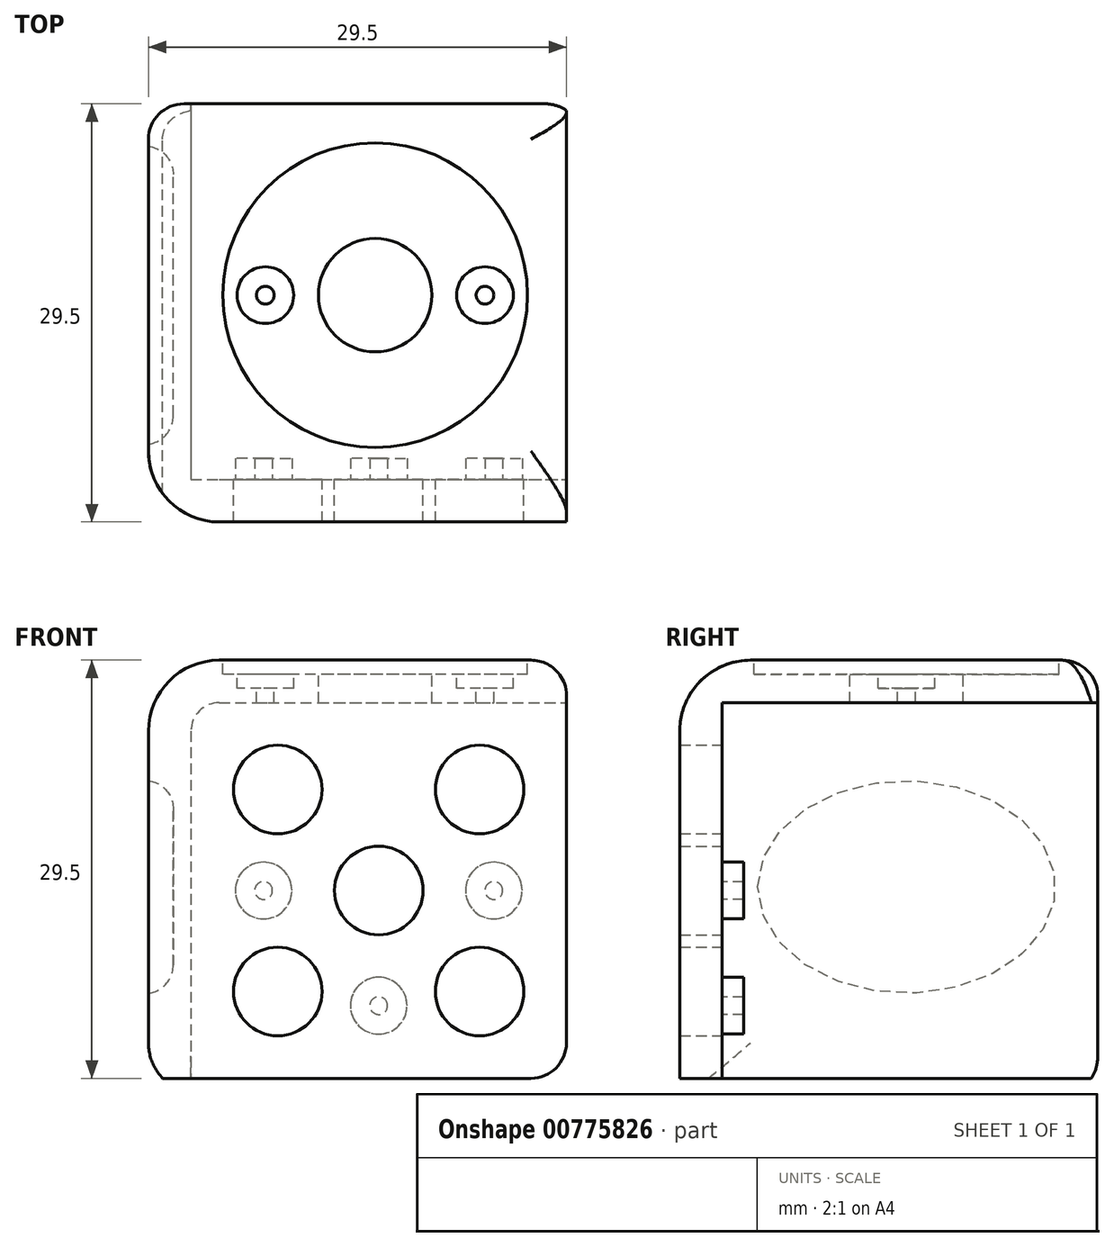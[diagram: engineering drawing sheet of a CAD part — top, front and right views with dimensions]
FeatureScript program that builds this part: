
annotation { "Feature Type Name" : "Feature", "Feature Type Description" : "" }
export const myFeature = defineFeature(function(context is Context, id is Id, definition is map)
    precondition{}
    {
        {
            var Q0;
            Q0=qCreatedBy(makeId("Front.planeOp"),FACE);
            var sketch = newSketch(context, id + "F0", { "sketchPlane" : qUnion([Q0])});
            skLineSegment(sketch, "E0.bottom", {"start": v(-9.8, 24) * mm, "end": v(13.7, 24) * mm});
            skLineSegment(sketch, "E0.top", {"start": v(-14.8, -5.5) * mm, "end": v(12.2, -5.5) * mm});
            skLineSegment(sketch, "E0.left", {"start": v(-14.8, 19) * mm, "end": v(-14.8, -5.5) * mm});
            skLineSegment(sketch, "E0.right", {"start": v(14.7, 23) * mm, "end": v(14.7, -3) * mm});
            skPoint(sketch, "E1", {"position": v(-9.3, 24) * mm});
            skPoint(sketch, "E2", {"position": v(-14.8, 18.5) * mm});
            skPoint(sketch, "E3", {"position": v(-14.8, -3) * mm});
            skPoint(sketch, "E4", {"position": v(-9.3, -5.5) * mm});
            skPoint(sketch, "E5", {"position": v(12.2, -5.5) * mm});
            skPoint(sketch, "E6", {"position": v(14.7, -3) * mm});
            skPoint(sketch, "E7", {"position": v(14.7, 18.5) * mm});
            skPoint(sketch, "E8", {"position": v(12.2, 24) * mm});
            skLineSegment(sketch, "E9", {"start": v(-9.3, 24) * mm, "end": v(-9.3, -5.5) * mm});
            skLineSegment(sketch, "E10", {"start": v(-14.8, -3) * mm, "end": v(14.7, -3) * mm});
            skLineSegment(sketch, "E11", {"start": v(12.2, -5.5) * mm, "end": v(12.2, 24) * mm});
            skLineSegment(sketch, "E12", {"start": v(14.7, 18.5) * mm, "end": v(-14.8, 18.5) * mm});
            skPoint(sketch, "E13", {"position": v(-9.3, 18.5) * mm});
            skPoint(sketch, "E14", {"position": v(12.2, 18.5) * mm});
            skPoint(sketch, "E15", {"position": v(-9.3, -3) * mm});
            skPoint(sketch, "E16", {"position": v(12.2, -3) * mm});
            skCircle(sketch, "E17", {"center": v(-5.67, 14.88) * mm, "radius": 3.12 * mm});
            skCircle(sketch, "E18", {"center": v(8.58, 14.88) * mm, "radius": 3.12 * mm});
            skCircle(sketch, "E19", {"center": v(-5.67, 0.62) * mm, "radius": 3.12 * mm});
            skCircle(sketch, "E20", {"center": v(8.58, 0.62) * mm, "radius": 3.12 * mm});
            skCircle(sketch, "E21", {"center": v(1.46, 7.75) * mm, "radius": 3.12 * mm});
            skPoint(sketch, "E22.visualSharp", {"position": v(-14.8, 24) * mm});
            skArc(sketch, "E22.filletArc", {"start": v(-9.8, 24) * mm, "mid": v(-13.33, 22.54) * mm, "end": v(-14.8, 19) * mm});
            skPoint(sketch, "E23", {"position": v(14.7, 23) * mm});
            skArc(sketch, "E24", {"start": v(14.7, 23) * mm, "mid": v(13.55, 23.74) * mm, "end": v(12.2, 24) * mm});
            skPoint(sketch, "E25", {"position": v(-13.8, -5.5) * mm});
            skArc(sketch, "E26", {"start": v(-14.8, -3) * mm, "mid": v(-14.53, -4.35) * mm, "end": v(-13.8, -5.5) * mm});
            skPoint(sketch, "E27.visualSharp", {"position": v(14.7, -5.5) * mm});
            skArc(sketch, "E27.filletArc", {"start": v(12.2, -5.5) * mm, "mid": v(13.98, -4.77) * mm, "end": v(14.7, -3) * mm});
            skSolve(sketch);
        }
        {
            var Q0;
            {var subQ7=sQuery(id+"F0.wireOp",EDGE,"E22.filletArc");Q0=makeQuery(id+"F0.imprint","IMPRINT",FACE,{"disambiguationData":[TD([[makeQuery(id+"F0.imprint","IMPRINT",EDGE,{"derivedFrom":subQ7}),1.0]])]});}
            var Q1;
            {var subQ0=sQuery(id+"F0.wireOp",EDGE,"E9");var subQ1=sQuery(id+"F0.wireOp",EDGE,"E0.bottom");var subQ2=makeQuery(id+"F0.imprint","INTERSECT",VERTEX,{"derivedFrom":[subQ1,subQ0]});Q1=makeQuery(id+"F0.imprint","IMPRINT",FACE,{"disambiguationData":[TD([[makeQuery(id+"F0.imprint","IMPRINT",EDGE,{"disambiguationData":[TD([[subQ2,-1.0]])],"derivedFrom":subQ0}),1.0]])]});}
            var Q2;
            {var subQ0=sQuery(id+"F0.wireOp",EDGE,"E24");Q2=makeQuery(id+"F0.imprint","IMPRINT",FACE,{"disambiguationData":[TD([[makeQuery(id+"F0.imprint","IMPRINT",EDGE,{"derivedFrom":subQ0}),1.0]])]});}
            var Q3;
            {var subQ0=sQuery(id+"F0.wireOp",EDGE,"E10");var subQ5=sQuery(id+"F0.wireOp",EDGE,"E11");var subQ7=makeQuery(id+"F0.imprint","INTERSECT",VERTEX,{"derivedFrom":[subQ0,subQ5]});Q3=makeQuery(id+"F0.imprint","IMPRINT",FACE,{"disambiguationData":[TD([[makeQuery(id+"F0.imprint","IMPRINT",EDGE,{"disambiguationData":[TD([[subQ7,-1.0]])],"derivedFrom":subQ5}),-1.0]])]});}
            var Q4;
            Q4=makeQuery(id+"F0.imprint","IMPRINT",FACE,{"disambiguationData":[TD([[makeQuery(id+"F0.imprint","IMPRINT",EDGE,{"derivedFrom":sQuery(id+"F0.wireOp",EDGE,"E17")}),-1.0]])]});
            var Q5;
            {var subQ3=sQuery(id+"F0.wireOp",EDGE,"E12");var subQ5=sQuery(id+"F0.wireOp",EDGE,"E9");var subQ6=makeQuery(id+"F0.imprint","INTERSECT",VERTEX,{"derivedFrom":[subQ5,subQ3]});Q5=makeQuery(id+"F0.imprint","IMPRINT",FACE,{"disambiguationData":[TD([[makeQuery(id+"F0.imprint","IMPRINT",EDGE,{"disambiguationData":[TD([[subQ6,-1.0]])],"derivedFrom":subQ5}),-1.0]])]});}
            var Q6;
            {var subQ3=sQuery(id+"F0.wireOp",EDGE,"E26");Q6=makeQuery(id+"F0.imprint","IMPRINT",FACE,{"disambiguationData":[TD([[makeQuery(id+"F0.imprint","IMPRINT",EDGE,{"derivedFrom":subQ3}),1.0]])]});}
            var Q7;
            {var subQ1=sQuery(id+"F0.wireOp",EDGE,"E0.top");var subQ3=sQuery(id+"F0.wireOp",EDGE,"E9");var subQ4=makeQuery(id+"F0.imprint","INTERSECT",VERTEX,{"derivedFrom":[subQ1,subQ3]});Q7=makeQuery(id+"F0.imprint","IMPRINT",FACE,{"disambiguationData":[TD([[makeQuery(id+"F0.imprint","IMPRINT",EDGE,{"disambiguationData":[TD([[subQ4,1.0]])],"derivedFrom":subQ3}),1.0]])]});}
            var Q8;
            {var subQ0=sQuery(id+"F0.wireOp",EDGE,"E27.filletArc");Q8=makeQuery(id+"F0.imprint","IMPRINT",FACE,{"disambiguationData":[TD([[makeQuery(id+"F0.imprint","IMPRINT",EDGE,{"derivedFrom":subQ0}),1.0]])]});}
            extrude(context, id + "F1", {"entities" : qUnion([Q0, Q1, Q2, Q3, Q4, Q5, Q6, Q7, Q8]), "depth" : 3 * mm, "offsetDistance" : 25 * mm});
        }
        {
            var Q0;
            Q0=makeQuery(id+"F1.opExtrude","CAP_FACE",FACE,{"disambiguationData":[OSD([sQuery(id+"F0.wireOp",EDGE,"E0.bottom"),sQuery(id+"F0.wireOp",EDGE,"E0.top"),sQuery(id+"F0.wireOp",EDGE,"E0.left"),sQuery(id+"F0.wireOp",EDGE,"E0.right"),sQuery(id+"F0.wireOp",EDGE,"E17"),sQuery(id+"F0.wireOp",EDGE,"E18"),sQuery(id+"F0.wireOp",EDGE,"E19"),sQuery(id+"F0.wireOp",EDGE,"E20"),sQuery(id+"F0.wireOp",EDGE,"E21"),sQuery(id+"F0.wireOp",EDGE,"E22.filletArc"),sQuery(id+"F0.wireOp",EDGE,"E24"),sQuery(id+"F0.wireOp",EDGE,"E26"),sQuery(id+"F0.wireOp",EDGE,"E27.filletArc")])],"isStart":true});
            var sketch = newSketch(context, id + "F2", { "sketchPlane" : qUnion([Q0])});
            skPoint(sketch, "E28", {"position": v(11.8, -3) * mm});
            skPoint(sketch, "E29", {"position": v(-12.2, 21) * mm});
            skLineSegment(sketch, "E30", {"start": v(-12.2, 21) * mm, "end": v(9.8, 21) * mm});
            skLineSegment(sketch, "E31", {"start": v(11.8, 19) * mm, "end": v(11.8, -3) * mm});
            skLineSegment(sketch, "E32", {"start": v(11.8, -3) * mm, "end": v(11.8, -5.5) * mm});
            skLineSegment(sketch, "E33", {"start": v(-12.2, 21) * mm, "end": v(-14.7, 21) * mm});
            skPoint(sketch, "E34.visualSharp", {"position": v(11.8, 21) * mm});
            skArc(sketch, "E34.filletArc", {"start": v(11.8, 19) * mm, "mid": v(11.2, 20.41) * mm, "end": v(9.8, 21) * mm});
            skSolve(sketch);
        }
        {
            var Q0;
            Q0=makeQuery(id+"F2.imprint","IMPRINT",FACE,{"disambiguationData":[TD([[makeQuery(id+"F2.imprint","IMPRINT",EDGE,{"derivedFrom":sQuery(id+"F2.wireOp",EDGE,"E30")}),1.0]])]});
            extrude(context, id + "F3", {"entities" : qUnion([Q0]), "operationType" : NewBodyOperationType.ADD, "depth" : 26.5 * mm, "offsetDistance" : 25 * mm});
        }
        {
            var Q0;
            Q0=makeQuery(id+"F1.opExtrude","CAP_EDGE",EDGE,{"disambiguationData":[OSD([sQuery(id+"F0.wireOp",EDGE,"E0.bottom")])],"isStart":false});
            var Q1;
            Q1=makeQuery(id+"F1.opExtrude","CAP_EDGE",EDGE,{"disambiguationData":[OSD([sQuery(id+"F0.wireOp",EDGE,"E0.left")])],"isStart":false});
            var Q2;
            Q2=makeQuery(id+"F1.opExtrude","CAP_EDGE",EDGE,{"disambiguationData":[OSD([sQuery(id+"F0.wireOp",EDGE,"E22.filletArc")])],"isStart":false});
            fillet(context, id + "F4", {"entities" : qUnion([Q0, Q1, Q2]), "radius" : 5 * mm, "tangentPropagation" : true, "allowEdgeOverflow" : false});
        }
        {
            var Q0;
            {var subQ0=sQuery(id+"F0.wireOp",EDGE,"E24");var subQ1=sQuery(id+"F0.wireOp",EDGE,"E0.right");Q0=makeQuery(id+"F3.boolean.opBoolean","MERGE",EDGE,{"derivedFrom":[makeQuery(id+"F1.opExtrude","SWEPT_EDGE",EDGE,{"disambiguationData":[OSD([subQ1,subQ0])]}),makeQuery(id+"F3.opExtrude","SWEPT_EDGE",EDGE,{"disambiguationData":[OSD([subQ1,subQ0])]})]});}
            var Q1;
            Q1=makeQuery(id+"F3.opExtrude","CAP_EDGE",EDGE,{"disambiguationData":[OSD([sQuery(id+"F0.wireOp",EDGE,"E0.bottom")])],"isStart":false});
            var Q2;
            Q2=makeQuery(id+"F3.opExtrude","CAP_EDGE",EDGE,{"disambiguationData":[OSD([sQuery(id+"F0.wireOp",EDGE,"E24")])],"isStart":false});
            fillet(context, id + "F5", {"entities" : qUnion([Q0, Q1, Q2]), "radius" : 2.5 * mm, "tangentPropagation" : true, "allowEdgeOverflow" : false});
        }
        {
            var Q0;
            {var subQ0=sQuery(id+"F0.wireOp",EDGE,"E0.bottom");Q0=makeQuery(id+"F3.boolean.opBoolean","MERGE",FACE,{"derivedFrom":[makeQuery(id+"F1.opExtrude","SWEPT_FACE",FACE,{"disambiguationData":[OSD([subQ0])]}),makeQuery(id+"F3.opExtrude","SWEPT_FACE",FACE,{"disambiguationData":[OSD([subQ0])]})]});}
            var sketch = newSketch(context, id + "F6", { "sketchPlane" : qUnion([Q0])});
            skLineSegment(sketch, "E35", {"start": v(1.2, 24) * mm, "end": v(1.2, 2) * mm});
            skLineSegment(sketch, "E36", {"start": v(-9.8, 13) * mm, "end": v(12.2, 13) * mm});
            skCircle(sketch, "E37", {"center": v(1.2, 13) * mm, "radius": 10.75 * mm});
            skSolve(sketch);
        }
        {
            var Q0;
            {var subQ0=sQuery(id+"F6.wireOp",EDGE,"E36");var subQ1=sQuery(id+"F6.wireOp",EDGE,"E35");var subQ2=makeQuery(id+"F6.imprint","INTERSECT",VERTEX,{"derivedFrom":[subQ1,subQ0]});Q0=makeQuery(id+"F6.imprint","IMPRINT",FACE,{"disambiguationData":[TD([[makeQuery(id+"F6.imprint","IMPRINT",EDGE,{"disambiguationData":[TD([[subQ2,-1.0]])],"derivedFrom":subQ1}),-1.0]])]});}
            var Q1;
            {var subQ0=sQuery(id+"F6.wireOp",EDGE,"E37");var subQ1=sQuery(id+"F6.wireOp",EDGE,"E35");var subQ2=makeQuery(id+"F6.imprint","INTERSECT",VERTEX,{"disambiguationData":[OD(0.0)],"derivedFrom":[subQ1,subQ0]});Q1=makeQuery(id+"F6.imprint","IMPRINT",FACE,{"disambiguationData":[TD([[makeQuery(id+"F6.imprint","IMPRINT",EDGE,{"disambiguationData":[TD([[subQ2,-1.0]])],"derivedFrom":subQ1}),-1.0]])]});}
            var Q2;
            {var subQ0=sQuery(id+"F6.wireOp",EDGE,"E37");var subQ1=sQuery(id+"F6.wireOp",EDGE,"E35");var subQ2=makeQuery(id+"F6.imprint","INTERSECT",VERTEX,{"disambiguationData":[OD(0.0)],"derivedFrom":[subQ1,subQ0]});Q2=makeQuery(id+"F6.imprint","IMPRINT",FACE,{"disambiguationData":[TD([[makeQuery(id+"F6.imprint","IMPRINT",EDGE,{"disambiguationData":[TD([[subQ2,-1.0]])],"derivedFrom":subQ1}),1.0]])]});}
            var Q3;
            {var subQ0=sQuery(id+"F6.wireOp",EDGE,"E36");var subQ1=sQuery(id+"F6.wireOp",EDGE,"E35");var subQ2=makeQuery(id+"F6.imprint","INTERSECT",VERTEX,{"derivedFrom":[subQ1,subQ0]});Q3=makeQuery(id+"F6.imprint","IMPRINT",FACE,{"disambiguationData":[TD([[makeQuery(id+"F6.imprint","IMPRINT",EDGE,{"disambiguationData":[TD([[subQ2,-1.0]])],"derivedFrom":subQ1}),1.0]])]});}
            extrude(context, id + "F7", {"entities" : qUnion([Q0, Q1, Q2, Q3]), "operationType" : NewBodyOperationType.REMOVE, "oppositeDirection" : true, "depth" : 1 * mm, "offsetDistance" : 25 * mm});
        }
        {
            var Q0;
            Q0=makeQuery(id+"F7.boolean.opBoolean","COPY",FACE,{"derivedFrom":makeQuery(id+"F7.opExtrude","CAP_FACE",FACE,{"disambiguationData":[OSD([sQuery(id+"F6.wireOp",EDGE,"E37")])],"isStart":false})});
            var sketch = newSketch(context, id + "F8", { "sketchPlane" : qUnion([Q0])});
            skCircle(sketch, "E38", {"center": v(1.2, 13) * mm, "radius": 4 * mm});
            skCircle(sketch, "E39", {"center": v(-6.54, 13) * mm, "radius": 2 * mm});
            skCircle(sketch, "E40", {"center": v(8.96, 13) * mm, "radius": 2 * mm});
            skCircle(sketch, "E41", {"center": v(-6.54, 13) * mm, "radius": 0.62 * mm});
            skCircle(sketch, "E42", {"center": v(8.96, 13) * mm, "radius": 0.62 * mm});
            skSolve(sketch);
        }
        {
            var Q0;
            Q0=makeQuery(id+"F8.imprint","IMPRINT",FACE,{"disambiguationData":[TD([[makeQuery(id+"F8.imprint","IMPRINT",EDGE,{"derivedFrom":sQuery(id+"F8.wireOp",EDGE,"E38")}),1.0]])]});
            extrude(context, id + "F9", {"entities" : qUnion([Q0]), "operationType" : NewBodyOperationType.REMOVE, "oppositeDirection" : true, "depth" : 25 * mm, "offsetDistance" : 25 * mm});
        }
        {
            var Q0;
            Q0=makeQuery(id+"F8.imprint","IMPRINT",FACE,{"disambiguationData":[TD([[makeQuery(id+"F8.imprint","IMPRINT",EDGE,{"derivedFrom":sQuery(id+"F8.wireOp",EDGE,"E39")}),1.0]])]});
            extrude(context, id + "F10", {"entities" : qUnion([Q0]), "operationType" : NewBodyOperationType.REMOVE, "oppositeDirection" : true, "depth" : 1 * mm, "offsetDistance" : 25 * mm});
        }
        {
            var Q0;
            Q0=makeQuery(id+"F8.imprint","IMPRINT",FACE,{"disambiguationData":[TD([[makeQuery(id+"F8.imprint","IMPRINT",EDGE,{"derivedFrom":sQuery(id+"F8.wireOp",EDGE,"E40")}),1.0]])]});
            extrude(context, id + "F11", {"entities" : qUnion([Q0]), "operationType" : NewBodyOperationType.REMOVE, "oppositeDirection" : true, "depth" : 1 * mm, "offsetDistance" : 25 * mm});
        }
        {
            var Q0;
            Q0=makeQuery(id+"F8.imprint","IMPRINT",FACE,{"disambiguationData":[TD([[makeQuery(id+"F8.imprint","IMPRINT",EDGE,{"derivedFrom":sQuery(id+"F8.wireOp",EDGE,"E41")}),1.0]])]});
            extrude(context, id + "F12", {"entities" : qUnion([Q0]), "operationType" : NewBodyOperationType.REMOVE, "oppositeDirection" : true, "depth" : 25 * mm, "offsetDistance" : 25 * mm});
        }
        {
            var Q0;
            Q0=makeQuery(id+"F8.imprint","IMPRINT",FACE,{"disambiguationData":[TD([[makeQuery(id+"F8.imprint","IMPRINT",EDGE,{"derivedFrom":sQuery(id+"F8.wireOp",EDGE,"E42")}),1.0]])]});
            extrude(context, id + "F13", {"entities" : qUnion([Q0]), "operationType" : NewBodyOperationType.REMOVE, "oppositeDirection" : true, "depth" : 25 * mm, "offsetDistance" : 25 * mm});
        }
        {
            var Q0;
            {var subQ0=sQuery(id+"F0.wireOp",EDGE,"E0.left");Q0=makeQuery(id+"F3.boolean.opBoolean","MERGE",FACE,{"derivedFrom":[makeQuery(id+"F1.opExtrude","SWEPT_FACE",FACE,{"disambiguationData":[OSD([subQ0])]}),makeQuery(id+"F3.opExtrude","SWEPT_FACE",FACE,{"disambiguationData":[OSD([subQ0])]})]});}
            var sketch = newSketch(context, id + "F14", { "sketchPlane" : qUnion([Q0])});
            skLineSegment(sketch, "E43", {"start": v(-13, 19) * mm, "end": v(-13, -3) * mm});
            skLineSegment(sketch, "E44", {"start": v(-24, 8) * mm, "end": v(-2, 8) * mm});
            skEllipse(sketch, "E45", {"center": v(-13, 8) * mm, "majorRadius": 10.5 * mm, "minorRadius": 7.5 * mm, "majorAxis": v(1, 0)});
            skSolve(sketch);
        }
        {
            var Q0;
            {var subQ0=sQuery(id+"F14.wireOp",EDGE,"E45");var subQ1=sQuery(id+"F14.wireOp",EDGE,"E43");var subQ2=makeQuery(id+"F14.imprint","INTERSECT",VERTEX,{"disambiguationData":[OD(0.0)],"derivedFrom":[subQ1,subQ0]});Q0=makeQuery(id+"F14.imprint","IMPRINT",FACE,{"disambiguationData":[TD([[makeQuery(id+"F14.imprint","IMPRINT",EDGE,{"disambiguationData":[TD([[subQ2,-1.0]])],"derivedFrom":subQ1}),-1.0]])]});}
            var Q1;
            {var subQ0=sQuery(id+"F14.wireOp",EDGE,"E45");var subQ1=sQuery(id+"F14.wireOp",EDGE,"E43");var subQ2=makeQuery(id+"F14.imprint","INTERSECT",VERTEX,{"disambiguationData":[OD(0.0)],"derivedFrom":[subQ1,subQ0]});Q1=makeQuery(id+"F14.imprint","IMPRINT",FACE,{"disambiguationData":[TD([[makeQuery(id+"F14.imprint","IMPRINT",EDGE,{"disambiguationData":[TD([[subQ2,-1.0]])],"derivedFrom":subQ1}),1.0]])]});}
            var Q2;
            {var subQ0=sQuery(id+"F14.wireOp",EDGE,"E44");var subQ1=sQuery(id+"F14.wireOp",EDGE,"E43");var subQ2=makeQuery(id+"F14.imprint","INTERSECT",VERTEX,{"derivedFrom":[subQ1,subQ0]});Q2=makeQuery(id+"F14.imprint","IMPRINT",FACE,{"disambiguationData":[TD([[makeQuery(id+"F14.imprint","IMPRINT",EDGE,{"disambiguationData":[TD([[subQ2,-1.0]])],"derivedFrom":subQ1}),1.0]])]});}
            var Q3;
            {var subQ0=sQuery(id+"F14.wireOp",EDGE,"E44");var subQ1=sQuery(id+"F14.wireOp",EDGE,"E43");var subQ2=makeQuery(id+"F14.imprint","INTERSECT",VERTEX,{"derivedFrom":[subQ1,subQ0]});Q3=makeQuery(id+"F14.imprint","IMPRINT",FACE,{"disambiguationData":[TD([[makeQuery(id+"F14.imprint","IMPRINT",EDGE,{"disambiguationData":[TD([[subQ2,-1.0]])],"derivedFrom":subQ1}),-1.0]])]});}
            extrude(context, id + "F15", {"entities" : qUnion([Q0, Q1, Q2, Q3]), "operationType" : NewBodyOperationType.REMOVE, "oppositeDirection" : true, "depth" : 1.75 * mm, "offsetDistance" : 25 * mm});
        }
        {
            var Q0;
            Q0=makeQuery(id+"F15.boolean.opBoolean","COPY",EDGE,{"derivedFrom":makeQuery(id+"F15.opExtrude","CAP_EDGE",EDGE,{"disambiguationData":[OSD([sQuery(id+"F14.wireOp",EDGE,"E45")])],"isStart":false})});
            fillet(context, id + "F16", {"entities" : qUnion([Q0]), "radius" : 2 * mm, "tangentPropagation" : true, "allowEdgeOverflow" : false});
        }
        {
            var Q0;
            Q0=makeQuery(id+"F1.opExtrude","CAP_FACE",FACE,{"disambiguationData":[OSD([sQuery(id+"F0.wireOp",EDGE,"E0.bottom"),sQuery(id+"F0.wireOp",EDGE,"E0.top"),sQuery(id+"F0.wireOp",EDGE,"E0.left"),sQuery(id+"F0.wireOp",EDGE,"E0.right"),sQuery(id+"F0.wireOp",EDGE,"E17"),sQuery(id+"F0.wireOp",EDGE,"E18"),sQuery(id+"F0.wireOp",EDGE,"E19"),sQuery(id+"F0.wireOp",EDGE,"E20"),sQuery(id+"F0.wireOp",EDGE,"E21"),sQuery(id+"F0.wireOp",EDGE,"E22.filletArc"),sQuery(id+"F0.wireOp",EDGE,"E24"),sQuery(id+"F0.wireOp",EDGE,"E26"),sQuery(id+"F0.wireOp",EDGE,"E27.filletArc")])],"isStart":true});
            var sketch = newSketch(context, id + "F17", { "sketchPlane" : qUnion([Q0])});
            skCircle(sketch, "E46", {"center": v(-1.46, 15.88) * mm, "radius": 2 * mm});
            skCircle(sketch, "E47", {"center": v(-1.46, 15.88) * mm, "radius": 0.62 * mm});
            skCircle(sketch, "E48", {"center": v(-9.58, 7.75) * mm, "radius": 2 * mm});
            skCircle(sketch, "E49", {"center": v(-9.58, 7.75) * mm, "radius": 0.62 * mm});
            skCircle(sketch, "E50", {"center": v(-1.46, -0.37) * mm, "radius": 2 * mm});
            skCircle(sketch, "E51", {"center": v(-1.46, -0.37) * mm, "radius": 0.62 * mm});
            skCircle(sketch, "E52", {"center": v(6.67, 7.75) * mm, "radius": 2 * mm});
            skCircle(sketch, "E53", {"center": v(6.67, 7.75) * mm, "radius": 0.62 * mm});
            skSolve(sketch);
        }
        {
            var Q0;
            Q0=makeQuery(id+"F17.imprint","IMPRINT",FACE,{"disambiguationData":[TD([[makeQuery(id+"F17.imprint","IMPRINT",EDGE,{"derivedFrom":sQuery(id+"F17.wireOp",EDGE,"E46")}),1.0]])]});
            var sketch = newSketch(context, id + "F18", { "sketchPlane" : qUnion([Q0])});
            skSolve(sketch);
        }
        {
            var Q0;
            Q0=makeQuery(id+"F18.imprint","IMPRINT",FACE,{"disambiguationData":[TD([[makeQuery(id+"F18.imprint","IMPRINT",EDGE,{"derivedFrom":makeQuery(id+"F17.imprint","IMPRINT",EDGE,{"derivedFrom":sQuery(id+"F17.wireOp",EDGE,"E46")})}),1.0]])]});
            var Q1;
            Q1=makeQuery(id+"F17.imprint","IMPRINT",FACE,{"disambiguationData":[TD([[makeQuery(id+"F17.imprint","IMPRINT",EDGE,{"derivedFrom":sQuery(id+"F17.wireOp",EDGE,"E48")}),1.0]])]});
            var Q2;
            Q2=makeQuery(id+"F17.imprint","IMPRINT",FACE,{"disambiguationData":[TD([[makeQuery(id+"F17.imprint","IMPRINT",EDGE,{"derivedFrom":sQuery(id+"F17.wireOp",EDGE,"E50")}),1.0]])]});
            var Q3;
            Q3=makeQuery(id+"F17.imprint","IMPRINT",FACE,{"disambiguationData":[TD([[makeQuery(id+"F17.imprint","IMPRINT",EDGE,{"derivedFrom":sQuery(id+"F17.wireOp",EDGE,"E52")}),1.0]])]});
            extrude(context, id + "F19", {"entities" : qUnion([Q0, Q1, Q2, Q3]), "operationType" : NewBodyOperationType.ADD, "depth" : 1.5 * mm, "offsetDistance" : 25 * mm});
        }
    });
